# Revit family: Basin-Wall-Caroma Liano Hand1
name_source: partatom
category: Plumbing Fixtures
revit_build: Autodesk Revit 2014 (Build: 20131024_2115(x64)
units: mm (PartAtom-declared; Revit-internal decimal feet)

## types (1)
- Liano - 1 Tap Hole
    1 Taphole = Yes
    3 Tapholes = No
    Assembly Code = D2010310
    CW Connection = No
    Default Elevation = 865 mm  [stored 2.83793 ft]
    Depth_ANZRS = 170 mm  [stored 0.557743 ft]
    Description = Caroma Liano Hand Wall Basin
    HW Connection = No
    Keynote = WB
    Length_ANZRS = 460 mm  [stored 1.50919 ft]
    Manufacturer = GWA Bathrooms & Kitchens
    Material_ANZRS = Porcelain-White-Caroma
    Model = 649715W
    ModifiedIssue_ANZRS = 20140919.01 $
    Spout Penetration = 0 mm  [stored 0 ft]
    Tap Penetrations = 100 mm  [stored 0.328084 ft]
    Type Comments = White Only, includes flush fitting white plug and waste, supplied with overflow, Capacity 2L
    URL = http://www.caroma.com.au
    Vent Connection = No
    WFU = 1
    Waste = Metal-Chrome-Caroma
    Waste Connection = Yes
    WasteOutlet_ANZRS = 0
    Width_ANZRS = 285 mm  [stored 0.935039 ft]

note: [stored X ft] marks values corroborated as IEEE doubles in the binary element streams (Revit-internal decimal feet)

## geometry (parser evidence)
native form markers: Blend x8, Sweep x1
no freeform markers — native parametric forms only
